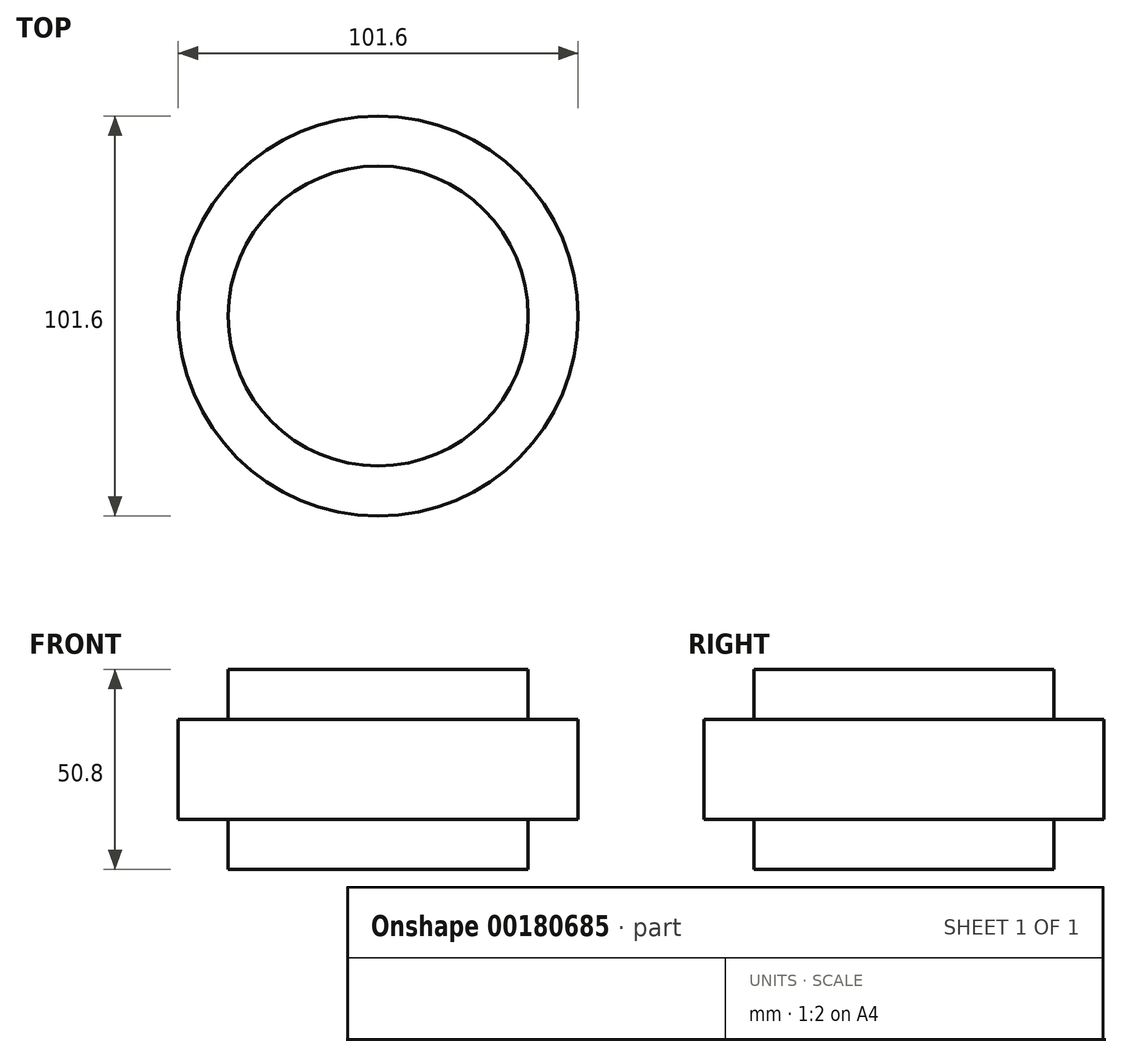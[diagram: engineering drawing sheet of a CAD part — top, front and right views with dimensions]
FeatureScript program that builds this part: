
annotation { "Feature Type Name" : "Feature", "Feature Type Description" : "" }
export const myFeature = defineFeature(function(context is Context, id is Id, definition is map)
    precondition{}
    {
        {
            var Q0;
            Q0=qCreatedBy(makeId("Top.planeOp"),FACE);
            var sketch = newSketch(context, id + "F0", { "sketchPlane" : qUnion([Q0])});
            skCircle(sketch, "E0", {"center": v(0, 0) * mm, "radius": 50.8 * mm});
            skCircle(sketch, "E1", {"center": v(0, 0) * mm, "radius": 38.1 * mm});
            skSolve(sketch);
        }
        {
            var Q0;
            Q0=makeQuery(id+"F0.imprint","IMPRINT",FACE,{"disambiguationData":[TD([[makeQuery(id+"F0.imprint","IMPRINT",EDGE,{"derivedFrom":sQuery(id+"F0.wireOp",EDGE,"E1")}),1.0]])]});
            extrude(context, id + "F1", {"entities" : qUnion([Q0]), "endBound" : BoundingType.SYMMETRIC, "depth" : 50.8 * mm});
        }
        {
            var Q0;
            Q0 = qSketchRegion(id + "F0", true);
            extrude(context, id + "F2", {"entities" : qUnion([Q0]), "operationType" : NewBodyOperationType.ADD, "endBound" : BoundingType.SYMMETRIC, "depth" : 25.4 * mm});
        }
    });
